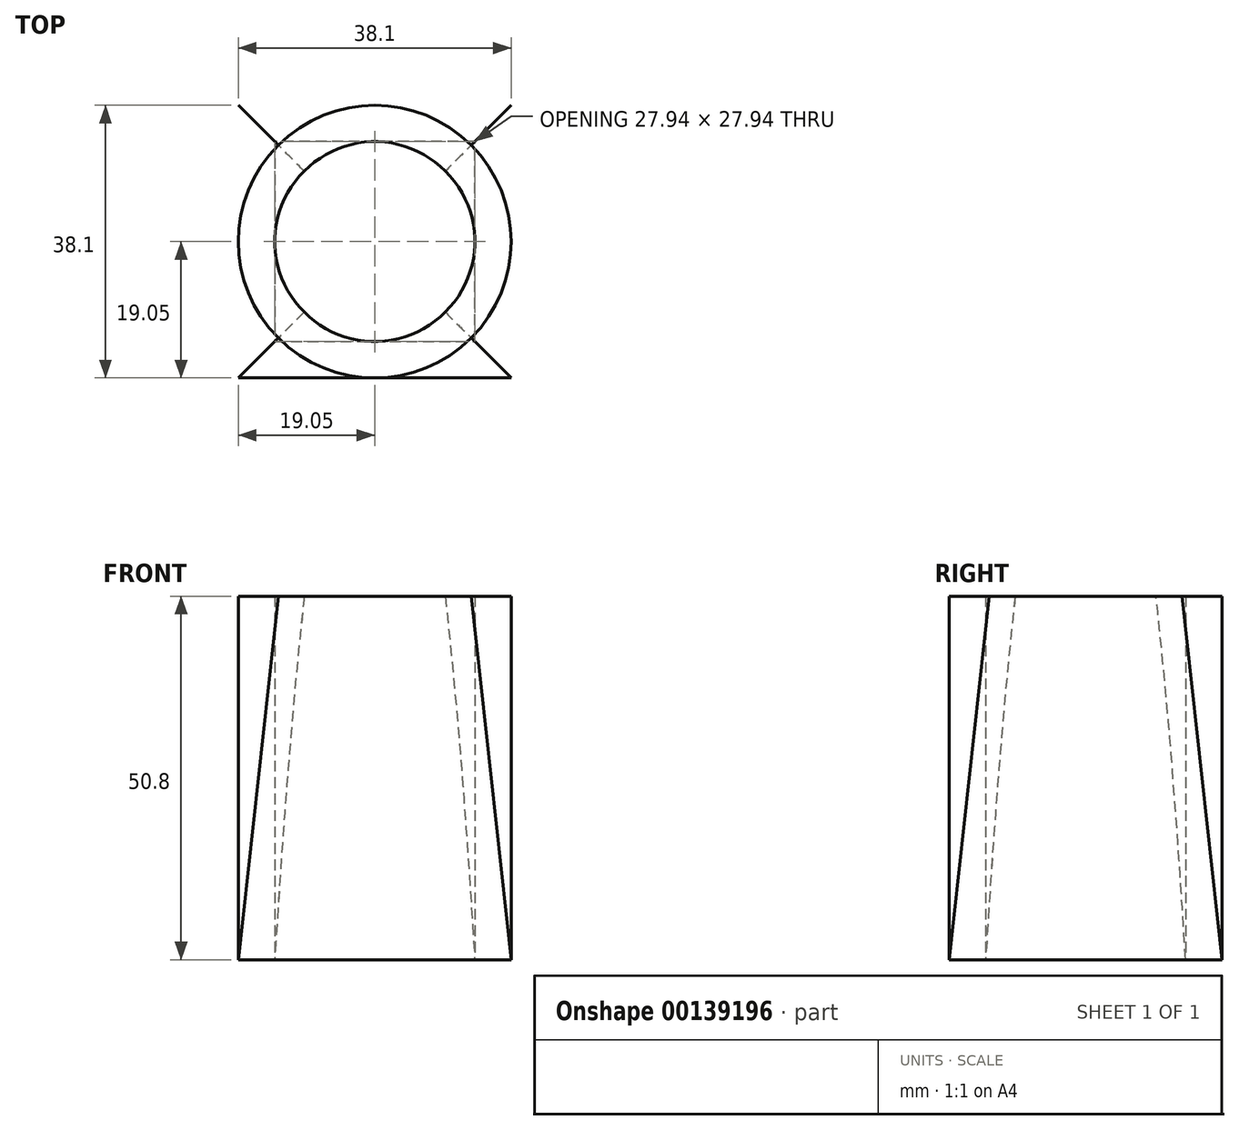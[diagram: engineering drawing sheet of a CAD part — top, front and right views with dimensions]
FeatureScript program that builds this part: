
annotation { "Feature Type Name" : "Feature", "Feature Type Description" : "" }
export const myFeature = defineFeature(function(context is Context, id is Id, definition is map)
    precondition{}
    {
        {
            var Q0;
            Q0=qCreatedBy(makeId("Front.planeOp"),FACE);
            var sketch = newSketch(context, id + "F0", { "sketchPlane" : qUnion([Q0])});
            skLineSegment(sketch, "E0", {"start": v(19.05, 0) * mm, "end": v(19.05, 50.8) * mm});
            skSolve(sketch);
        }
        {
            var Q0;
            Q0=qCreatedBy(makeId("Top.planeOp"),FACE);
            var sketch = newSketch(context, id + "F1", { "sketchPlane" : qUnion([Q0])});
            skLineSegment(sketch, "E1.bottom", {"start": v(19.05, 19.05) * mm, "end": v(-19.05, 19.05) * mm});
            skLineSegment(sketch, "E1.top", {"start": v(19.05, -19.05) * mm, "end": v(-19.05, -19.05) * mm});
            skLineSegment(sketch, "E1.left", {"start": v(19.05, 19.05) * mm, "end": v(19.05, -19.05) * mm});
            skLineSegment(sketch, "E1.right", {"start": v(-19.05, 19.05) * mm, "end": v(-19.05, -19.05) * mm});
            skPoint(sketch, "E1.middle", {"position": v(0, 0) * mm});
            skSolve(sketch);
        }
        {
            var Q0;
            Q0=qCreatedBy(makeId("Top.planeOp"),FACE);
            var Q1;
            Q1=sQuery(id+"F0.wireOp",VERTEX,"E0.end");
            cPlane(context, id + "F2", {"entities" : qUnion([Q0, Q1]), "cplaneType" : CPlaneType.PLANE_POINT, "offset" : 25.4 * mm, "width" : 152.4 * mm, "height" : 152.4 * mm});
        }
        {
            var Q0;
            Q0=qCreatedBy(id+"F2.planeOp",FACE);
            var sketch = newSketch(context, id + "F3", { "sketchPlane" : qUnion([Q0])});
            skCircle(sketch, "E2", {"center": v(0, 0) * mm, "radius": 19.05 * mm});
            skSolve(sketch);
        }
        {
            var Q0;
            Q0=makeQuery(id+"F1.imprint","IMPRINT",FACE,{"disambiguationData":[TD([[makeQuery(id+"F1.imprint","IMPRINT",EDGE,{"derivedFrom":sQuery(id+"F1.wireOp",EDGE,"E1.bottom")}),1.0]])]});
            var Q1;
            Q1=makeQuery(id+"F3.imprint","IMPRINT",FACE,{"disambiguationData":[TD([[makeQuery(id+"F3.imprint","IMPRINT",EDGE,{"derivedFrom":sQuery(id+"F3.wireOp",EDGE,"E2")}),1.0]])]});
            loft(context, id + "F4", {"sheetProfilesArray" : [{ "sheetProfileEntities" : qUnion([Q0]) }, { "sheetProfileEntities" : qUnion([Q1]) }]});
        }
        {
            var Q0;
            Q0=makeQuery(id+"F4.opLoft","CAP_FACE",FACE,{"disambiguationData":[OSD([makeQuery(id+"F3.imprint","IMPRINT",FACE,{"disambiguationData":[TD([[makeQuery(id+"F3.imprint","IMPRINT",EDGE,{"derivedFrom":sQuery(id+"F3.wireOp",EDGE,"E2")}),1.0]])]})])],"isStart":true});
            var Q1;
            Q1=makeQuery(id+"F4.opLoft","CAP_FACE",FACE,{"disambiguationData":[OSD([makeQuery(id+"F1.imprint","IMPRINT",FACE,{"disambiguationData":[TD([[makeQuery(id+"F1.imprint","IMPRINT",EDGE,{"derivedFrom":sQuery(id+"F1.wireOp",EDGE,"E1.bottom")}),1.0]])]})])],"isStart":true});
            shell(context, id + "F5", {"entities" : qUnion([Q0, Q1]), "thickness" : 5.08 * mm});
        }
    });
